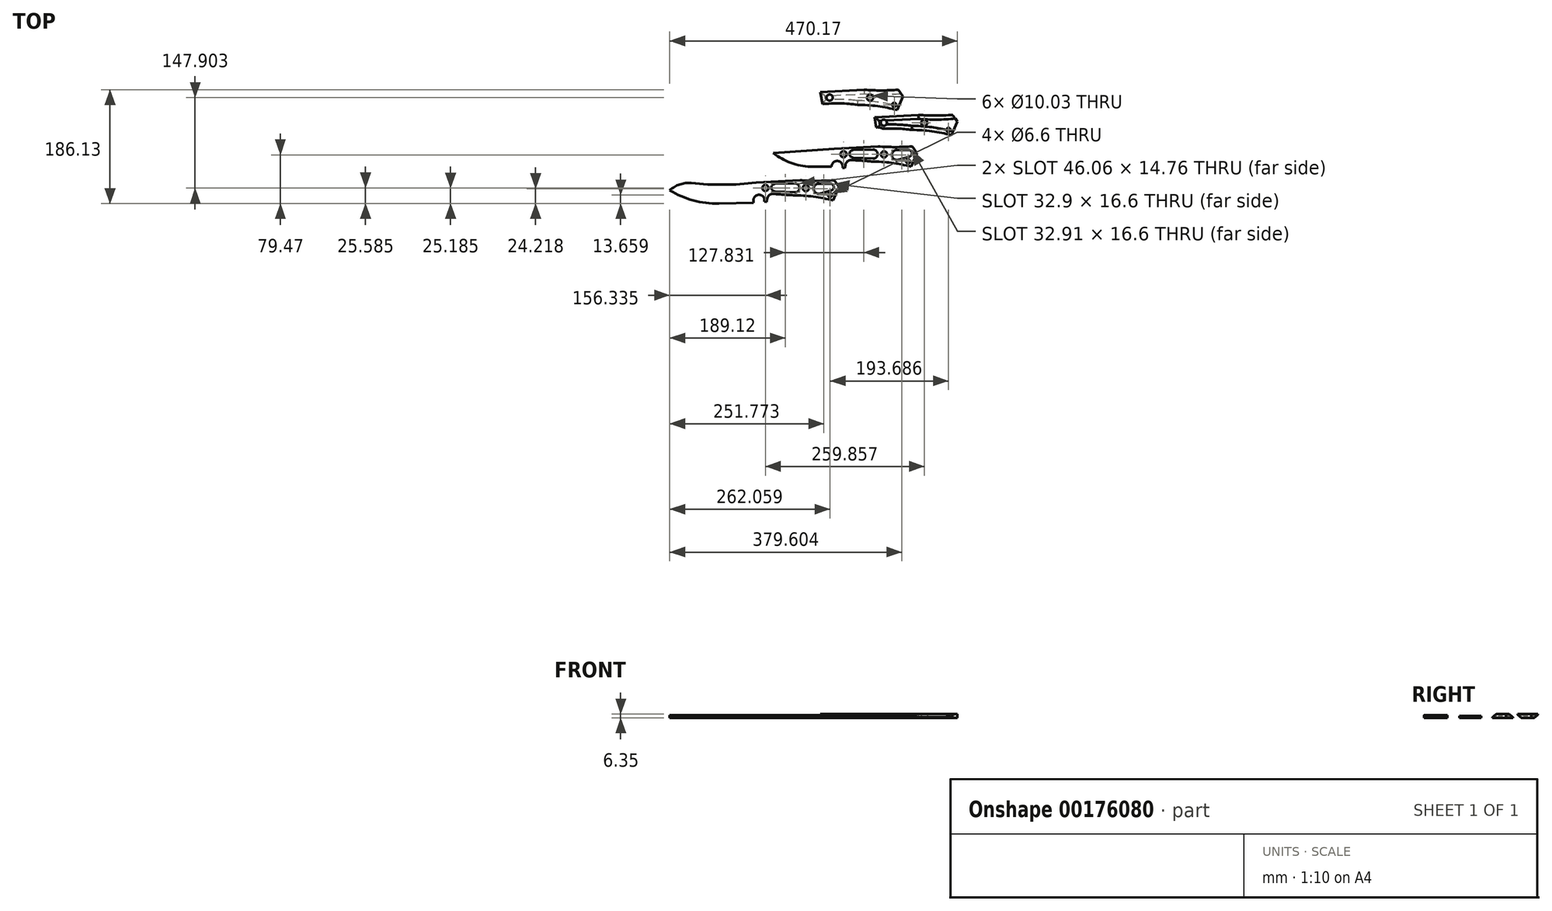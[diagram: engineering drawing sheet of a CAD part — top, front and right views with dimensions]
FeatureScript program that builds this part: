
annotation { "Feature Type Name" : "Feature", "Feature Type Description" : "" }
export const myFeature = defineFeature(function(context is Context, id is Id, definition is map)
    precondition{}
    {
        {
            var Q0;
            Q0=qCreatedBy(makeId("Top.planeOp"),FACE);
            var sketch = newSketch(context, id + "F0", { "sketchPlane" : qUnion([Q0])});
            skLineSegment(sketch, "E0", {"start": v(121.58, 13.5) * mm, "end": v(113.75, 24.57) * mm});
            skLineSegment(sketch, "E1", {"start": v(121.58, 13.5) * mm, "end": v(111.98, -8.6) * mm});
            skArc(sketch, "E2", {"start": v(111.98, -8.6) * mm, "mid": v(79.86, -2.33) * mm, "end": v(47.22, -0.03) * mm});
            skArc(sketch, "E3", {"start": v(57.98, 24.57) * mm, "mid": v(85.87, 23.43) * mm, "end": v(113.75, 24.57) * mm});
            skLineSegment(sketch, "E4", {"start": v(-13.78, 20.8) * mm, "end": v(57.98, 24.57) * mm});
            skLineSegment(sketch, "E5", {"start": v(-113.37, 13.5) * mm, "end": v(-13.78, 20.8) * mm});
            skArc(sketch, "E6", {"start": v(-113.37, 13.5) * mm, "mid": v(-84.75, -2.33) * mm, "end": v(-52.67, -8.62) * mm});
            skLineSegment(sketch, "E7", {"start": v(-52.67, -8.62) * mm, "end": v(-18.04, -8.62) * mm});
            skCircle(sketch, "E8", {"center": v(1.44, 11.74) * mm, "radius": 5.02 * mm});
            skCircle(sketch, "E9", {"center": v(67.6, 11.53) * mm, "radius": 5.02 * mm});
            skLineSegment(sketch, "E10", {"start": v(17.2, 18.49) * mm, "end": v(49.68, 19.3) * mm});
            skLineSegment(sketch, "E11", {"start": v(17.23, 6.16) * mm, "end": v(49.5, 4.55) * mm});
            skLineSegment(sketch, "E12", {"start": v(89.75, 2.26) * mm, "end": v(109.59, 8.19) * mm});
            skLineSegment(sketch, "E13", {"start": v(108.07, 18.6) * mm, "end": v(88.86, 18.86) * mm});
            skCircle(sketch, "E14", {"center": v(107.16, 0) * mm, "radius": 3.3 * mm});
            skArc(sketch, "E15", {"start": v(109.59, 8.19) * mm, "mid": v(113.33, 14.05) * mm, "end": v(108.07, 18.6) * mm});
            skArc(sketch, "E16", {"start": v(88.86, 18.86) * mm, "mid": v(80.42, 10.08) * mm, "end": v(89.75, 2.26) * mm});
            skArc(sketch, "E17", {"start": v(49.5, 4.55) * mm, "mid": v(57.25, 11.83) * mm, "end": v(49.68, 19.3) * mm});
            skArc(sketch, "E18", {"start": v(17.2, 18.49) * mm, "mid": v(11.2, 12.31) * mm, "end": v(17.23, 6.16) * mm});
            skArc(sketch, "E19", {"start": v(0, -8.62) * mm, "mid": v(-9.02, 0.68) * mm, "end": v(-18.04, -8.62) * mm});
            skLineSegment(sketch, "E20", {"start": v(0, -8.62) * mm, "end": v(0, -10.68) * mm});
            skLineSegment(sketch, "E21", {"start": v(0, -10.68) * mm, "end": v(3.55, -11.25) * mm});
            skLineSegment(sketch, "E22", {"start": v(3.55, -11.25) * mm, "end": v(4.42, -5.77) * mm});
            skArc(sketch, "E23", {"start": v(13.25, 2.25) * mm, "mid": v(7.43, -0.2) * mm, "end": v(4.42, -5.77) * mm});
            skArc(sketch, "E24", {"start": v(47.22, -0.03) * mm, "mid": v(30.24, 1.3) * mm, "end": v(13.25, 2.25) * mm});
            skSolve(sketch);
        }
        {
            var Q0;
            Q0 = qSketchRegion(id + "F0", true);
            extrude(context, id + "F1", {"entities" : qUnion([Q0]), "depth" : 3.17 * mm});
        }
        {
            var Q0;
            Q0=qCreatedBy(makeId("Top.planeOp"),FACE);
            var sketch = newSketch(context, id + "F2", { "sketchPlane" : qUnion([Q0])});
            skLineSegment(sketch, "E25", {"start": v(187.44, 65.06) * mm, "end": v(179.6, 76.13) * mm});
            skLineSegment(sketch, "E26", {"start": v(187.44, 65.06) * mm, "end": v(177.84, 42.96) * mm});
            skArc(sketch, "E27", {"start": v(177.84, 42.96) * mm, "mid": v(145.72, 49.23) * mm, "end": v(113.07, 51.53) * mm});
            skArc(sketch, "E28", {"start": v(113.07, 51.53) * mm, "mid": v(80.55, 53.82) * mm, "end": v(48.03, 51.6) * mm});
            skArc(sketch, "E29", {"start": v(123.83, 76.13) * mm, "mid": v(151.72, 75) * mm, "end": v(179.6, 76.13) * mm});
            skLineSegment(sketch, "E30", {"start": v(52.08, 72.36) * mm, "end": v(123.83, 76.13) * mm});
            skLineSegment(sketch, "E31", {"start": v(-47.51, 65.06) * mm, "end": v(52.08, 72.36) * mm});
            skArc(sketch, "E32", {"start": v(-47.51, 65.06) * mm, "mid": v(-18.9, 49.24) * mm, "end": v(13.19, 42.94) * mm});
            skLineSegment(sketch, "E33", {"start": v(13.19, 42.94) * mm, "end": v(47.82, 42.94) * mm});
            skArc(sketch, "E34", {"start": v(55.51, 52.5) * mm, "mid": v(50.01, 49.05) * mm, "end": v(47.82, 42.94) * mm});
            skLineSegment(sketch, "E35", {"start": v(55.51, 52.5) * mm, "end": v(52.08, 72.36) * mm});
            skCircle(sketch, "E36", {"center": v(67.3, 63.3) * mm, "radius": 5.02 * mm});
            skCircle(sketch, "E37", {"center": v(133.46, 63.09) * mm, "radius": 5.02 * mm});
            skLineSegment(sketch, "E38", {"start": v(83.06, 70.05) * mm, "end": v(115.53, 70.87) * mm});
            skLineSegment(sketch, "E39", {"start": v(83.08, 57.72) * mm, "end": v(115.35, 56.1) * mm});
            skLineSegment(sketch, "E40", {"start": v(155.6, 53.82) * mm, "end": v(175.44, 59.75) * mm});
            skLineSegment(sketch, "E41", {"start": v(173.92, 70.15) * mm, "end": v(154.71, 70.42) * mm});
            skCircle(sketch, "E42", {"center": v(173.01, 51.56) * mm, "radius": 3.3 * mm});
            skArc(sketch, "E43", {"start": v(175.44, 59.75) * mm, "mid": v(179.18, 65.6) * mm, "end": v(173.92, 70.15) * mm});
            skArc(sketch, "E44", {"start": v(154.71, 70.42) * mm, "mid": v(146.28, 61.65) * mm, "end": v(155.6, 53.82) * mm});
            skArc(sketch, "E45", {"start": v(115.35, 56.1) * mm, "mid": v(123.1, 63.4) * mm, "end": v(115.53, 70.87) * mm});
            skArc(sketch, "E46", {"start": v(83.06, 70.05) * mm, "mid": v(77.05, 63.88) * mm, "end": v(83.08, 57.72) * mm});
            skArc(sketch, "E47", {"start": v(68.2, 42.94) * mm, "mid": v(58, 52.47) * mm, "end": v(47.82, 42.94) * mm});
            skArc(sketch, "E48", {"start": v(65.94, 53.38) * mm, "mid": v(60.64, 55.48) * mm, "end": v(54.94, 55.78) * mm});
            skSolve(sketch);
        }
        {
            var Q0;
            Q0=makeQuery(id+"F2.imprint","IMPRINT",FACE,{"disambiguationData":[TD([[makeQuery(id+"F2.imprint","IMPRINT",EDGE,{"derivedFrom":sQuery(id+"F2.wireOp",EDGE,"E25")}),1.0]])]});
            var Q1;
            Q1=makeQuery(id+"F2.imprint","IMPRINT",FACE,{"disambiguationData":[TD([[makeQuery(id+"F2.imprint","IMPRINT",EDGE,{"derivedFrom":sQuery(id+"F2.wireOp",EDGE,"E38")}),-1.0]])]});
            var Q2;
            Q2=makeQuery(id+"F2.imprint","IMPRINT",FACE,{"disambiguationData":[TD([[makeQuery(id+"F2.imprint","IMPRINT",EDGE,{"derivedFrom":sQuery(id+"F2.wireOp",EDGE,"E40")}),1.0]])]});
            extrude(context, id + "F3", {"entities" : qUnion([Q0, Q1, Q2]), "depth" : 6.35 * mm});
        }
        {
            var Q0;
            Q0=makeQuery(id+"F3.opExtrude","CAP_EDGE",EDGE,{"disambiguationData":[OSD([sQuery(id+"F2.wireOp",EDGE,"E27")])],"isStart":false});
            var Q1;
            Q1=makeQuery(id+"F3.opExtrude","CAP_EDGE",EDGE,{"disambiguationData":[OSD([sQuery(id+"F2.wireOp",EDGE,"E28")])],"isStart":false});
            var Q2;
            Q2=makeQuery(id+"F3.opExtrude","CAP_EDGE",EDGE,{"disambiguationData":[OSD([sQuery(id+"F2.wireOp",EDGE,"E29")])],"isStart":false});
            var Q3;
            Q3=makeQuery(id+"F3.opExtrude","CAP_EDGE",EDGE,{"disambiguationData":[OSD([sQuery(id+"F2.wireOp",EDGE,"E30")])],"isStart":false});
            var Q4;
            Q4=makeQuery(id+"F3.opExtrude","CAP_EDGE",EDGE,{"disambiguationData":[OSD([sQuery(id+"F2.wireOp",EDGE,"E35")])],"isStart":false});
            chamfer(context, id + "F4", {"entities" : qUnion([Q0, Q1, Q2, Q3, Q4]), "chamferType" : ChamferType.TWO_OFFSETS, "width1" : 5.08 * mm, "oppositeDirection" : false, "width2" : 6.6 * mm, "tangentPropagation" : true});
        }
        {
            var Q0;
            Q0=qCreatedBy(makeId("Top.planeOp"),FACE);
            var sketch = newSketch(context, id + "F5", { "sketchPlane" : qUnion([Q0])});
            skLineSegment(sketch, "E49", {"start": v(98.78, 106.15) * mm, "end": v(90.95, 117.22) * mm});
            skLineSegment(sketch, "E50", {"start": v(98.78, 106.15) * mm, "end": v(89.18, 84.05) * mm});
            skArc(sketch, "E51", {"start": v(89.18, 84.05) * mm, "mid": v(57.06, 90.32) * mm, "end": v(24.41, 92.62) * mm});
            skArc(sketch, "E52", {"start": v(24.41, 92.62) * mm, "mid": v(-8.1, 94.9) * mm, "end": v(-40.63, 92.68) * mm});
            skArc(sketch, "E53", {"start": v(35.17, 117.22) * mm, "mid": v(63.06, 116.08) * mm, "end": v(90.95, 117.22) * mm});
            skLineSegment(sketch, "E54", {"start": v(-36.58, 113.45) * mm, "end": v(35.17, 117.22) * mm});
            skLineSegment(sketch, "E55", {"start": v(-136.17, 106.15) * mm, "end": v(-36.58, 113.45) * mm});
            skArc(sketch, "E56", {"start": v(-136.17, 106.15) * mm, "mid": v(-107.56, 90.33) * mm, "end": v(-75.47, 84.03) * mm});
            skLineSegment(sketch, "E57", {"start": v(-75.47, 84.03) * mm, "end": v(-40.84, 84.03) * mm});
            skArc(sketch, "E58", {"start": v(-33.15, 93.6) * mm, "mid": v(-38.65, 90.14) * mm, "end": v(-40.84, 84.03) * mm});
            skLineSegment(sketch, "E59", {"start": v(-33.15, 93.6) * mm, "end": v(-36.58, 113.45) * mm});
            skCircle(sketch, "E60", {"center": v(-21.37, 104.4) * mm, "radius": 5.02 * mm});
            skCircle(sketch, "E61", {"center": v(44.8, 104.18) * mm, "radius": 5.02 * mm});
            skLineSegment(sketch, "E62", {"start": v(-5.6, 111.14) * mm, "end": v(26.87, 111.96) * mm});
            skLineSegment(sketch, "E63", {"start": v(-5.58, 98.8) * mm, "end": v(26.69, 97.2) * mm});
            skLineSegment(sketch, "E64", {"start": v(66.94, 94.91) * mm, "end": v(86.78, 100.84) * mm});
            skLineSegment(sketch, "E65", {"start": v(85.26, 111.24) * mm, "end": v(66.05, 111.51) * mm});
            skCircle(sketch, "E66", {"center": v(84.35, 92.65) * mm, "radius": 3.3 * mm});
            skArc(sketch, "E67", {"start": v(86.78, 100.84) * mm, "mid": v(90.52, 106.7) * mm, "end": v(85.26, 111.24) * mm});
            skArc(sketch, "E68", {"start": v(66.05, 111.51) * mm, "mid": v(57.62, 102.73) * mm, "end": v(66.94, 94.91) * mm});
            skArc(sketch, "E69", {"start": v(26.69, 97.2) * mm, "mid": v(34.44, 104.48) * mm, "end": v(26.87, 111.96) * mm});
            skArc(sketch, "E70", {"start": v(-5.6, 111.14) * mm, "mid": v(-11.61, 104.96) * mm, "end": v(-5.58, 98.8) * mm});
            skSolve(sketch);
        }
        {
            var Q0;
            Q0=makeQuery(id+"F5.imprint","IMPRINT",FACE,{"disambiguationData":[TD([[makeQuery(id+"F5.imprint","IMPRINT",EDGE,{"derivedFrom":sQuery(id+"F5.wireOp",EDGE,"E49")}),1.0]])]});
            var Q1;
            Q1=makeQuery(id+"F5.imprint","IMPRINT",FACE,{"disambiguationData":[TD([[makeQuery(id+"F5.imprint","IMPRINT",EDGE,{"derivedFrom":sQuery(id+"F5.wireOp",EDGE,"E62")}),-1.0]])]});
            var Q2;
            Q2=makeQuery(id+"F5.imprint","IMPRINT",FACE,{"disambiguationData":[TD([[makeQuery(id+"F5.imprint","IMPRINT",EDGE,{"derivedFrom":sQuery(id+"F5.wireOp",EDGE,"E64")}),1.0]])]});
            extrude(context, id + "F6", {"entities" : qUnion([Q0, Q1, Q2]), "depth" : 6.35 * mm});
        }
        {
            var Q0;
            Q0=makeQuery(id+"F6.opExtrude","CAP_EDGE",EDGE,{"disambiguationData":[OSD([sQuery(id+"F5.wireOp",EDGE,"E51")])],"isStart":true});
            var Q1;
            Q1=makeQuery(id+"F6.opExtrude","CAP_EDGE",EDGE,{"disambiguationData":[OSD([sQuery(id+"F5.wireOp",EDGE,"E52")])],"isStart":true});
            var Q2;
            Q2=makeQuery(id+"F6.opExtrude","CAP_EDGE",EDGE,{"disambiguationData":[OSD([sQuery(id+"F5.wireOp",EDGE,"E54")])],"isStart":true});
            var Q3;
            Q3=makeQuery(id+"F6.opExtrude","CAP_EDGE",EDGE,{"disambiguationData":[OSD([sQuery(id+"F5.wireOp",EDGE,"E53")])],"isStart":true});
            var Q4;
            Q4=makeQuery(id+"F6.opExtrude","CAP_EDGE",EDGE,{"disambiguationData":[OSD([sQuery(id+"F5.wireOp",EDGE,"E59")])],"isStart":true});
            chamfer(context, id + "F7", {"entities" : qUnion([Q0, Q1, Q2, Q3, Q4]), "chamferType" : ChamferType.TWO_OFFSETS, "width1" : 6.6 * mm, "oppositeDirection" : false, "width2" : 5.08 * mm, "tangentPropagation" : true});
        }
        {
            var Q0;
            Q0=qCreatedBy(makeId("Top.planeOp"),FACE);
            var sketch = newSketch(context, id + "F8", { "sketchPlane" : qUnion([Q0])});
            skLineSegment(sketch, "E71", {"start": v(-6.25, -41.75) * mm, "end": v(-14.08, -30.68) * mm});
            skLineSegment(sketch, "E72", {"start": v(-6.25, -41.75) * mm, "end": v(-15.85, -63.86) * mm});
            skArc(sketch, "E73", {"start": v(-15.85, -63.86) * mm, "mid": v(-47.97, -57.58) * mm, "end": v(-80.61, -55.28) * mm});
            skArc(sketch, "E74", {"start": v(-69.85, -30.68) * mm, "mid": v(-41.96, -31.82) * mm, "end": v(-14.08, -30.68) * mm});
            skLineSegment(sketch, "E75", {"start": v(-141.6, -34.46) * mm, "end": v(-69.85, -30.68) * mm});
            skArc(sketch, "E76", {"start": v(-138.18, -54.3) * mm, "mid": v(-143.67, -57.76) * mm, "end": v(-145.87, -63.88) * mm});
            skLineSegment(sketch, "E77", {"start": v(-138.18, -54.3) * mm, "end": v(-141.6, -34.46) * mm});
            skCircle(sketch, "E78", {"center": v(-126.4, -43.5) * mm, "radius": 5.02 * mm});
            skCircle(sketch, "E79", {"center": v(-60.22, -43.73) * mm, "radius": 5.02 * mm});
            skLineSegment(sketch, "E80", {"start": v(-110.63, -36.76) * mm, "end": v(-78.15, -35.94) * mm});
            skLineSegment(sketch, "E81", {"start": v(-110.6, -49.1) * mm, "end": v(-78.34, -50.7) * mm});
            skLineSegment(sketch, "E82", {"start": v(-38.08, -53) * mm, "end": v(-18.24, -47.07) * mm});
            skLineSegment(sketch, "E83", {"start": v(-19.76, -36.66) * mm, "end": v(-38.97, -36.4) * mm});
            skCircle(sketch, "E84", {"center": v(-20.67, -55.25) * mm, "radius": 3.3 * mm});
            skArc(sketch, "E85", {"start": v(-18.24, -47.07) * mm, "mid": v(-14.5, -41.2) * mm, "end": v(-19.76, -36.66) * mm});
            skArc(sketch, "E86", {"start": v(-38.97, -36.4) * mm, "mid": v(-47.4, -45.17) * mm, "end": v(-38.08, -53) * mm});
            skArc(sketch, "E87", {"start": v(-78.34, -50.7) * mm, "mid": v(-70.58, -43.42) * mm, "end": v(-78.15, -35.94) * mm});
            skArc(sketch, "E88", {"start": v(-110.63, -36.76) * mm, "mid": v(-116.64, -42.94) * mm, "end": v(-110.6, -49.1) * mm});
            skArc(sketch, "E89", {"start": v(-127.83, -63.88) * mm, "mid": v(-136.85, -54.57) * mm, "end": v(-145.87, -63.88) * mm});
            skLineSegment(sketch, "E90", {"start": v(-127.83, -63.88) * mm, "end": v(-127.83, -65.93) * mm});
            skLineSegment(sketch, "E91", {"start": v(-127.83, -65.93) * mm, "end": v(-124.29, -66.5) * mm});
            skLineSegment(sketch, "E92", {"start": v(-124.29, -66.5) * mm, "end": v(-123.4, -61.02) * mm});
            skArc(sketch, "E93", {"start": v(-114.58, -53) * mm, "mid": v(-120.4, -55.46) * mm, "end": v(-123.4, -61.02) * mm});
            skLineSegment(sketch, "E94", {"start": v(-145.87, -63.88) * mm, "end": v(-145.73, -67.7) * mm});
            skLineSegment(sketch, "E95", {"start": v(-202.54, -68.88) * mm, "end": v(-145.73, -67.7) * mm});
            skArc(sketch, "E96", {"start": v(-282.73, -47.13) * mm, "mid": v(-244.2, -63.78) * mm, "end": v(-202.54, -68.88) * mm});
            skArc(sketch, "E97", {"start": v(-247.32, -35.34) * mm, "mid": v(-194.43, -38.12) * mm, "end": v(-141.6, -34.46) * mm});
            skArc(sketch, "E98", {"start": v(-247.32, -35.34) * mm, "mid": v(-266.23, -37.6) * mm, "end": v(-282.73, -47.13) * mm});
            skArc(sketch, "E99", {"start": v(-114.58, -53) * mm, "mid": v(-97.6, -54.24) * mm, "end": v(-80.61, -55.28) * mm});
            skSolve(sketch);
        }
        {
            var Q0;
            {var subQ1=sQuery(id+"F8.wireOp",EDGE,"E77");Q0=makeQuery(id+"F8.imprint","IMPRINT",FACE,{"disambiguationData":[TD([[makeQuery(id+"F8.imprint","IMPRINT",EDGE,{"derivedFrom":subQ1}),1.0]])]});}
            var Q1;
            {var subQ0=sQuery(id+"F8.wireOp",EDGE,"E90");Q1=makeQuery(id+"F8.imprint","IMPRINT",FACE,{"disambiguationData":[TD([[makeQuery(id+"F8.imprint","IMPRINT",EDGE,{"derivedFrom":subQ0}),1.0]])]});}
            var Q2;
            Q2=makeQuery(id+"F8.imprint","IMPRINT",FACE,{"disambiguationData":[TD([[makeQuery(id+"F8.imprint","IMPRINT",EDGE,{"derivedFrom":sQuery(id+"F8.wireOp",EDGE,"E71")}),1.0]])]});
            extrude(context, id + "F9", {"entities" : qUnion([Q0, Q1, Q2]), "depth" : 4.57 * mm});
        }
    });
